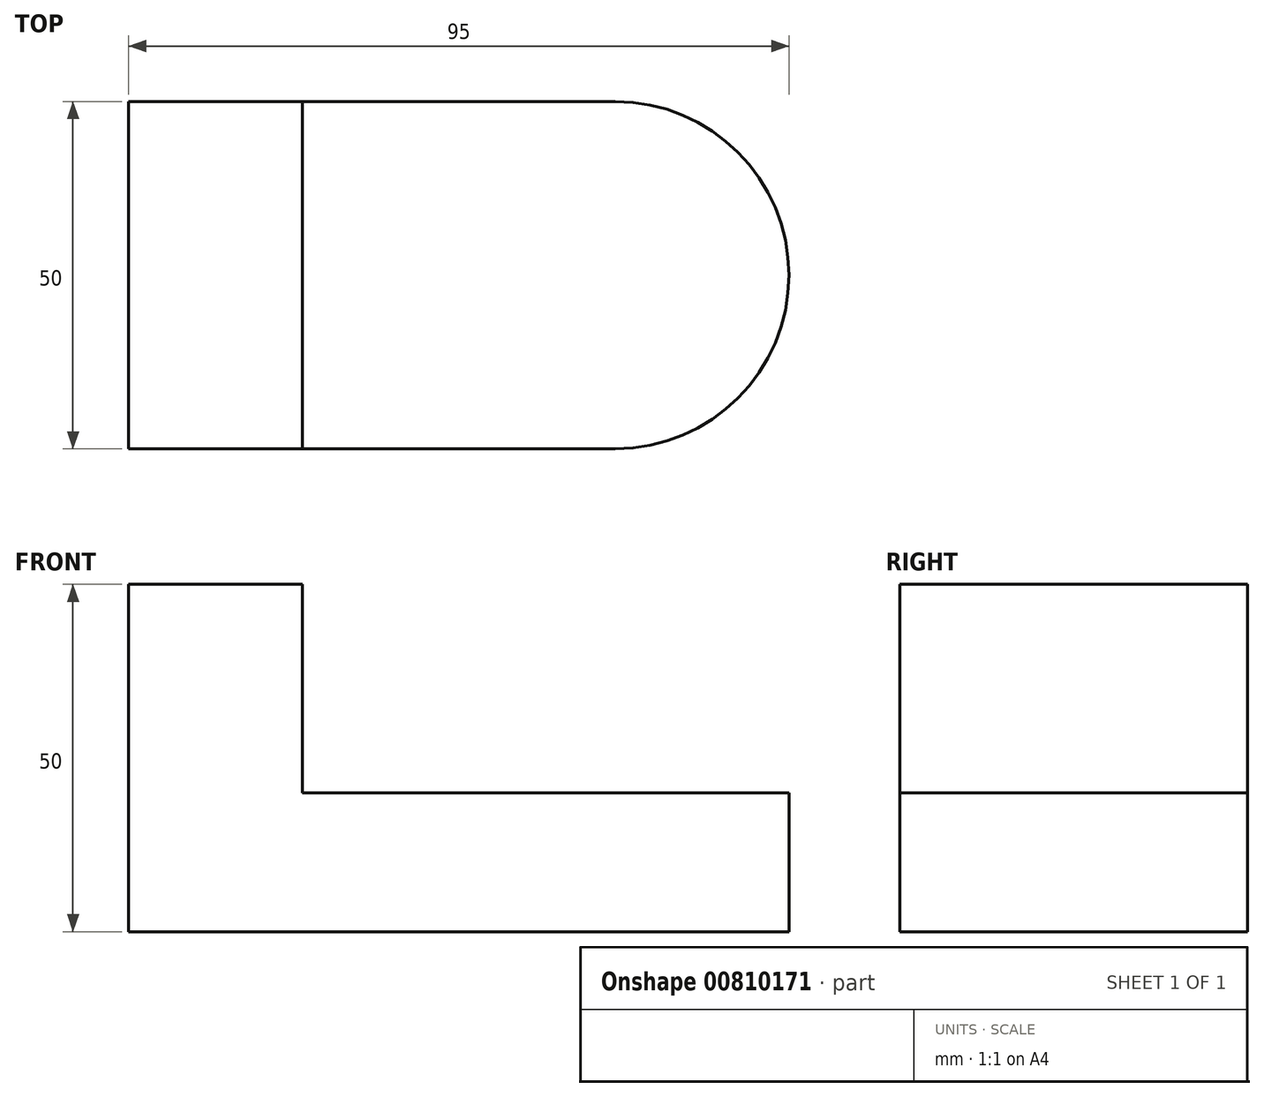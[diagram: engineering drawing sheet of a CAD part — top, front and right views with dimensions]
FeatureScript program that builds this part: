
annotation { "Feature Type Name" : "Feature", "Feature Type Description" : "" }
export const myFeature = defineFeature(function(context is Context, id is Id, definition is map)
    precondition{}
    {
        {
            var Q0;
            Q0=qCreatedBy(makeId("Top.planeOp"),FACE);
            var sketch = newSketch(context, id + "F0", { "sketchPlane" : qUnion([Q0])});
            skLineSegment(sketch, "E0.bottom", {"start": v(0, 0) * mm, "end": v(70, 0) * mm});
            skLineSegment(sketch, "E0.top", {"start": v(0, 50) * mm, "end": v(70, 50) * mm});
            skLineSegment(sketch, "E0.left", {"start": v(0, 0) * mm, "end": v(0, 50) * mm});
            skArc(sketch, "E1", {"start": v(70, 0) * mm, "mid": v(95, 25) * mm, "end": v(70, 50) * mm});
            skSolve(sketch);
        }
        {
            var Q0;
            Q0=makeQuery(id+"F0.imprint","IMPRINT",FACE,{"disambiguationData":[TD([[makeQuery(id+"F0.imprint","IMPRINT",EDGE,{"derivedFrom":sQuery(id+"F0.wireOp",EDGE,"E0.bottom")}),1.0]])]});
            extrude(context, id + "F1", {"entities" : qUnion([Q0]), "depth" : 20 * mm, "offsetDistance" : 25 * mm});
        }
        {
            var Q0;
            Q0=makeQuery(id+"F1.opExtrude","CAP_FACE",FACE,{"disambiguationData":[OSD([sQuery(id+"F0.wireOp",EDGE,"E0.bottom"),sQuery(id+"F0.wireOp",EDGE,"E0.top"),sQuery(id+"F0.wireOp",EDGE,"E0.left"),sQuery(id+"F0.wireOp",EDGE,"E1")])],"isStart":false});
            var sketch = newSketch(context, id + "F2", { "sketchPlane" : qUnion([Q0])});
            skLineSegment(sketch, "E2.bottom", {"start": v(0, 50) * mm, "end": v(25, 50) * mm});
            skLineSegment(sketch, "E2.top", {"start": v(0, 0) * mm, "end": v(25, 0) * mm});
            skLineSegment(sketch, "E2.left", {"start": v(0, 50) * mm, "end": v(0, 0) * mm});
            skLineSegment(sketch, "E2.right", {"start": v(25, 50) * mm, "end": v(25, 0) * mm});
            skSolve(sketch);
        }
        {
            var Q0;
            Q0=makeQuery(id+"F2.imprint","IMPRINT",FACE,{"disambiguationData":[TD([[makeQuery(id+"F2.imprint","IMPRINT",EDGE,{"derivedFrom":sQuery(id+"F2.wireOp",EDGE,"E2.bottom")}),-1.0]])]});
            extrude(context, id + "F3", {"entities" : qUnion([Q0]), "operationType" : NewBodyOperationType.ADD, "depth" : 30 * mm, "offsetDistance" : 25 * mm});
        }
    });
